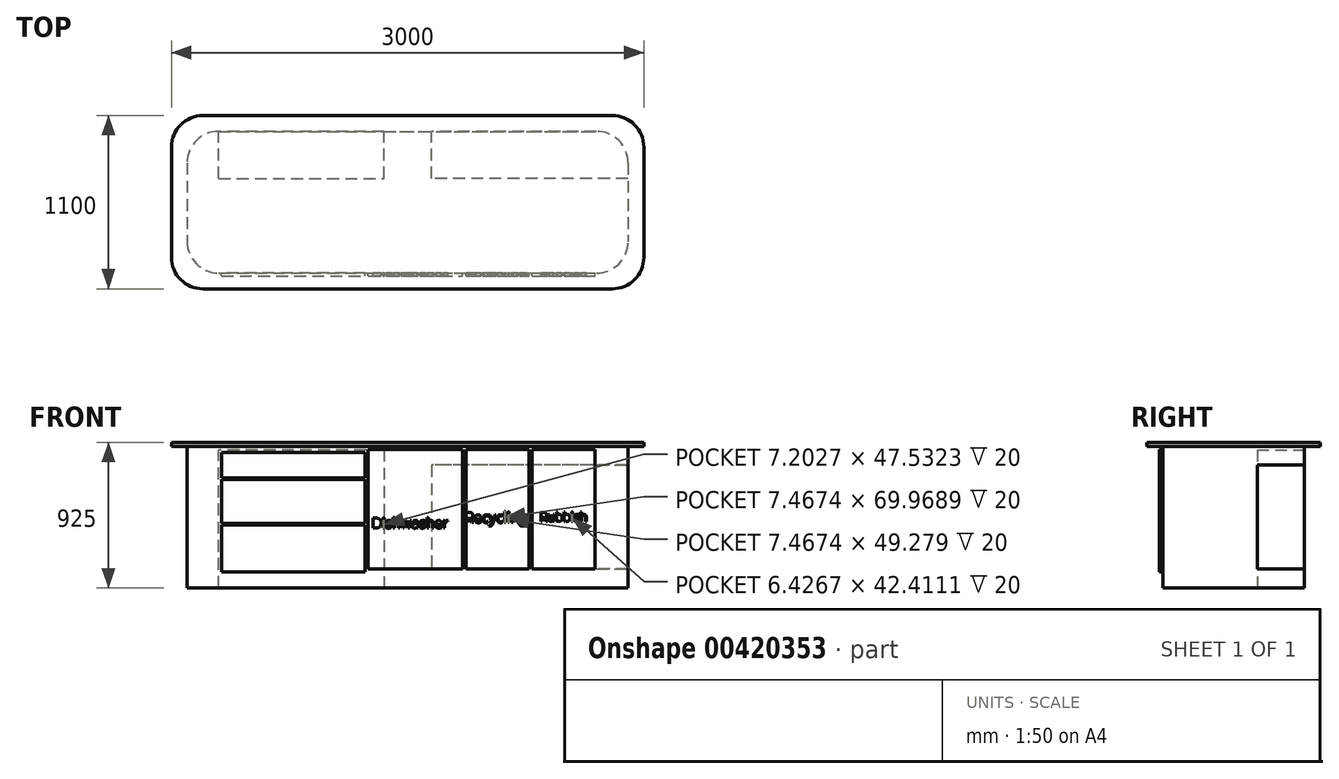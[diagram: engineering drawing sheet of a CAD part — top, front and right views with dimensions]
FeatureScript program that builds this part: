
annotation { "Feature Type Name" : "Feature", "Feature Type Description" : "" }
export const myFeature = defineFeature(function(context is Context, id is Id, definition is map)
    precondition{}
    {
        {
            var Q0;
            Q0=qCreatedBy(makeId("Top.planeOp"),FACE);
            var sketch = newSketch(context, id + "F0", { "sketchPlane" : qUnion([Q0])});
            skLineSegment(sketch, "E0", {"start": v(-1500, 0) * mm, "end": v(1500, 0) * mm, "construction": true});
            skLineSegment(sketch, "E1", {"start": v(0, 550) * mm, "end": v(0, -550) * mm, "construction": true});
            skLineSegment(sketch, "E2.bottom", {"start": v(-1300, 550) * mm, "end": v(1300, 550) * mm});
            skLineSegment(sketch, "E2.top", {"start": v(-1300, -550) * mm, "end": v(1300, -550) * mm});
            skLineSegment(sketch, "E2.left", {"start": v(-1500, 350) * mm, "end": v(-1500, -350) * mm});
            skLineSegment(sketch, "E2.right", {"start": v(1500, 350) * mm, "end": v(1500, -350) * mm});
            skPoint(sketch, "E3.visualSharp", {"position": v(-1500, 550) * mm});
            skPoint(sketch, "E4.visualSharp", {"position": v(1500, 550) * mm});
            skPoint(sketch, "E5.visualSharp", {"position": v(1500, -550) * mm});
            skPoint(sketch, "E6.visualSharp", {"position": v(-1500, -550) * mm});
            skLineSegment(sketch, "E7.bottom", {"start": v(-1200, 450) * mm, "end": v(1200, 450) * mm});
            skLineSegment(sketch, "E7.top", {"start": v(-1200, -450) * mm, "end": v(1200, -450) * mm});
            skLineSegment(sketch, "E7.left", {"start": v(-1400, 250) * mm, "end": v(-1400, -250) * mm});
            skLineSegment(sketch, "E7.right", {"start": v(1400, 250) * mm, "end": v(1400, -250) * mm});
            skPoint(sketch, "E8.visualSharp", {"position": v(1400, -450) * mm});
            skArc(sketch, "E8.filletArc", {"start": v(1200, -450) * mm, "mid": v(1341.42, -391.42) * mm, "end": v(1400, -250) * mm});
            skPoint(sketch, "E9.visualSharp", {"position": v(-1400, -450) * mm});
            skArc(sketch, "E9.filletArc", {"start": v(-1400, -250) * mm, "mid": v(-1341.42, -391.42) * mm, "end": v(-1200, -450) * mm});
            skPoint(sketch, "E10.visualSharp", {"position": v(1400, 450) * mm});
            skArc(sketch, "E10.filletArc", {"start": v(1400, 250) * mm, "mid": v(1341.42, 391.42) * mm, "end": v(1200, 450) * mm});
            skPoint(sketch, "E11.visualSharp", {"position": v(-1400, 450) * mm});
            skArc(sketch, "E11.filletArc", {"start": v(-1200, 450) * mm, "mid": v(-1341.42, 391.42) * mm, "end": v(-1400, 250) * mm});
            skArc(sketch, "E12.filletArc", {"start": v(1500, 350) * mm, "mid": v(1441.42, 491.42) * mm, "end": v(1300, 550) * mm});
            skArc(sketch, "E13.filletArc", {"start": v(1300, -550) * mm, "mid": v(1441.42, -491.42) * mm, "end": v(1500, -350) * mm});
            skArc(sketch, "E14.filletArc", {"start": v(-1500, -350) * mm, "mid": v(-1441.42, -491.42) * mm, "end": v(-1300, -550) * mm});
            skArc(sketch, "E15.filletArc", {"start": v(-1300, 550) * mm, "mid": v(-1441.42, 491.42) * mm, "end": v(-1500, 350) * mm});
            skSolve(sketch);
        }
        {
            var Q0;
            Q0=makeQuery(id+"F0.imprint","IMPRINT",FACE,{"disambiguationData":[TD([[makeQuery(id+"F0.imprint","IMPRINT",EDGE,{"derivedFrom":sQuery(id+"F0.wireOp",EDGE,"E7.bottom")}),-1.0]])]});
            extrude(context, id + "F1", {"entities" : qUnion([Q0]), "oppositeDirection" : true, "depth" : 900 * mm});
        }
        {
            var Q0;
            Q0=makeQuery(id+"F0.imprint","IMPRINT",FACE,{"disambiguationData":[TD([[makeQuery(id+"F0.imprint","IMPRINT",EDGE,{"derivedFrom":sQuery(id+"F0.wireOp",EDGE,"E2.bottom")}),-1.0]])]});
            var Q1;
            Q1=makeQuery(id+"F0.imprint","IMPRINT",FACE,{"disambiguationData":[TD([[makeQuery(id+"F0.imprint","IMPRINT",EDGE,{"derivedFrom":sQuery(id+"F0.wireOp",EDGE,"E7.bottom")}),-1.0]])]});
            extrude(context, id + "F2", {"entities" : qUnion([Q0, Q1]), "operationType" : NewBodyOperationType.ADD, "depth" : 25 * mm});
        }
        {
            var Q0;
            Q0=makeQuery(id+"F1.opExtrude","SWEPT_FACE",FACE,{"disambiguationData":[OSD([sQuery(id+"F0.wireOp",EDGE,"E7.top")])]});
            var sketch = newSketch(context, id + "F3", { "sketchPlane" : qUnion([Q0])});
            skLineSegment(sketch, "E16.bottom", {"start": v(-250, -20) * mm, "end": v(350, -20) * mm});
            skLineSegment(sketch, "E16.top", {"start": v(-250, -780) * mm, "end": v(350, -780) * mm});
            skLineSegment(sketch, "E16.left", {"start": v(-250, -20) * mm, "end": v(-250, -780) * mm});
            skLineSegment(sketch, "E16.right", {"start": v(350, -20) * mm, "end": v(350, -780) * mm});
            skLineSegment(sketch, "E17.bottom", {"start": v(-1160, -60) * mm, "end": v(-290, -60) * mm});
            skLineSegment(sketch, "E17.top", {"start": v(-1160, -180) * mm, "end": v(-290, -180) * mm});
            skLineSegment(sketch, "E17.left", {"start": v(-1160, -60) * mm, "end": v(-1160, -180) * mm});
            skLineSegment(sketch, "E17.right", {"start": v(-290, -60) * mm, "end": v(-290, -180) * mm});
            skLineSegment(sketch, "E18.bottom", {"start": v(-1160, -230) * mm, "end": v(-290, -230) * mm});
            skLineSegment(sketch, "E18.top", {"start": v(-1160, -470) * mm, "end": v(-290, -470) * mm});
            skLineSegment(sketch, "E18.left", {"start": v(-1160, -230) * mm, "end": v(-1160, -470) * mm});
            skLineSegment(sketch, "E18.right", {"start": v(-290, -230) * mm, "end": v(-290, -470) * mm});
            skLineSegment(sketch, "E19.bottom", {"start": v(-1160, -520) * mm, "end": v(-290, -520) * mm});
            skLineSegment(sketch, "E19.top", {"start": v(-1160, -780) * mm, "end": v(-290, -780) * mm});
            skLineSegment(sketch, "E19.left", {"start": v(-1160, -520) * mm, "end": v(-1160, -780) * mm});
            skLineSegment(sketch, "E19.right", {"start": v(-290, -520) * mm, "end": v(-290, -780) * mm});
            skLineSegment(sketch, "E20.bottom", {"start": v(-1180, -210) * mm, "end": v(-270, -210) * mm});
            skLineSegment(sketch, "E20.top", {"start": v(-1180, -490) * mm, "end": v(-270, -490) * mm});
            skLineSegment(sketch, "E20.left", {"start": v(-1180, -210) * mm, "end": v(-1180, -490) * mm});
            skLineSegment(sketch, "E20.right", {"start": v(-270, -210) * mm, "end": v(-270, -490) * mm});
            skLineSegment(sketch, "E21.bottom", {"start": v(-1180, -500) * mm, "end": v(-270, -500) * mm});
            skLineSegment(sketch, "E21.top", {"start": v(-1180, -800) * mm, "end": v(-270, -800) * mm});
            skLineSegment(sketch, "E21.left", {"start": v(-1180, -500) * mm, "end": v(-1180, -800) * mm});
            skLineSegment(sketch, "E21.right", {"start": v(-270, -500) * mm, "end": v(-270, -800) * mm});
            skLineSegment(sketch, "E22.bottom", {"start": v(-270, -200) * mm, "end": v(-1180, -200) * mm});
            skLineSegment(sketch, "E22.top", {"start": v(-270, -40) * mm, "end": v(-1180, -40) * mm});
            skLineSegment(sketch, "E22.left", {"start": v(-270, -200) * mm, "end": v(-270, -40) * mm});
            skLineSegment(sketch, "E22.right", {"start": v(-1180, -200) * mm, "end": v(-1180, -40) * mm});
            skLineSegment(sketch, "E23.bottom", {"start": v(-1200, -900) * mm, "end": v(-1200, -900) * mm});
            skLineSegment(sketch, "E23.top", {"start": v(-1200, -900) * mm, "end": v(-1200, -900) * mm});
            skLineSegment(sketch, "E23.left", {"start": v(-1200, -900) * mm, "end": v(-1200, -900) * mm});
            skLineSegment(sketch, "E23.right", {"start": v(-1200, -900) * mm, "end": v(-1200, -900) * mm});
            skLineSegment(sketch, "E24.top", {"start": v(-1200, -800) * mm, "end": v(-1200, -800) * mm});
            skLineSegment(sketch, "E24.left", {"start": v(-1200, -900) * mm, "end": v(-1200, -800) * mm});
            skLineSegment(sketch, "E24.right", {"start": v(-1200, -900) * mm, "end": v(-1200, -800) * mm});
            skText(sketch, "E25", { "text": "Dishwasher", "fontName": "OpenSans-Regular.ttf"});
            skLineSegment(sketch, "E26.bottom", {"start": v(370, -20) * mm, "end": v(770, -20) * mm});
            skLineSegment(sketch, "E26.top", {"start": v(370, -780) * mm, "end": v(770, -780) * mm});
            skLineSegment(sketch, "E26.left", {"start": v(370, -20) * mm, "end": v(370, -780) * mm});
            skLineSegment(sketch, "E26.right", {"start": v(770, -20) * mm, "end": v(770, -780) * mm});
            skLineSegment(sketch, "E27.bottom", {"start": v(790, -20) * mm, "end": v(1190, -20) * mm});
            skLineSegment(sketch, "E27.top", {"start": v(790, -780) * mm, "end": v(1190, -780) * mm});
            skLineSegment(sketch, "E27.left", {"start": v(790, -20) * mm, "end": v(790, -780) * mm});
            skLineSegment(sketch, "E27.right", {"start": v(1190, -20) * mm, "end": v(1190, -780) * mm});
            skText(sketch, "E28", { "text": "Recycling", "fontName": "OpenSans-Regular.ttf"});
            skText(sketch, "E29", { "text": "Rubbish", "fontName": "OpenSans-Regular.ttf"});
            const initialGuessF3  = {"E25": [-0.22795, -0.52, 1, 0, 0.06395], "E28": [0.36361, -0.48553, 1, 0, 0.0663], "E29": [0.84, -0.47629, 1, 0, 0.05706]};
            skSetInitialGuess(sketch, initialGuessF3);
            skSolve(sketch);
        }
        {
            var Q0;
            Q0=makeQuery(id+"F3.imprint","IMPRINT",FACE,{"disambiguationData":[TD([[makeQuery(id+"F3.imprint","IMPRINT",EDGE,{"derivedFrom":sQuery(id+"F3.wireOp",EDGE,"E16.bottom")}),-1.0]])]});
            var Q1;
            Q1=makeQuery(id+"F3.imprint","IMPRINT",FACE,{"disambiguationData":[TD([[makeQuery(id+"F3.imprint","IMPRINT",EDGE,{"derivedFrom":sQuery(id+"F3.wireOp",EDGE,"E26.bottom")}),-1.0]])]});
            var Q2;
            Q2=makeQuery(id+"F3.imprint","IMPRINT",FACE,{"disambiguationData":[TD([[makeQuery(id+"F3.imprint","IMPRINT",EDGE,{"derivedFrom":sQuery(id+"F3.wireOp",EDGE,"E27.bottom")}),-1.0]])]});
            var Q3;
            Q3=makeQuery(id+"F3.imprint","IMPRINT",FACE,{"disambiguationData":[TD([[makeQuery(id+"F3.imprint","IMPRINT",EDGE,{"derivedFrom":sQuery(id+"F3.wireOp",EDGE,"E18.bottom")}),-1.0]])]});
            var Q4;
            Q4=makeQuery(id+"F3.imprint","IMPRINT",FACE,{"disambiguationData":[TD([[makeQuery(id+"F3.imprint","IMPRINT",EDGE,{"derivedFrom":sQuery(id+"F3.wireOp",EDGE,"E17.bottom")}),-1.0]])]});
            var Q5;
            Q5=makeQuery(id+"F3.imprint","IMPRINT",FACE,{"disambiguationData":[TD([[makeQuery(id+"F3.imprint","IMPRINT",EDGE,{"derivedFrom":sQuery(id+"F3.wireOp",EDGE,"E19.bottom")}),-1.0]])]});
            var Q6;
            Q6=makeQuery(id+"F3.imprint","IMPRINT",FACE,{"disambiguationData":[TD([[makeQuery(id+"F3.imprint","IMPRINT",EDGE,{"derivedFrom":sQuery(id+"F3.wireOp",EDGE,"E19.bottom")}),1.0]])]});
            var Q7;
            Q7=makeQuery(id+"F3.imprint","IMPRINT",FACE,{"disambiguationData":[TD([[makeQuery(id+"F3.imprint","IMPRINT",EDGE,{"derivedFrom":sQuery(id+"F3.wireOp",EDGE,"E18.bottom")}),1.0]])]});
            var Q8;
            Q8=makeQuery(id+"F3.imprint","IMPRINT",FACE,{"disambiguationData":[TD([[makeQuery(id+"F3.imprint","IMPRINT",EDGE,{"derivedFrom":sQuery(id+"F3.wireOp",EDGE,"E17.bottom")}),1.0]])]});
            extrude(context, id + "F4", {"entities" : qUnion([Q0, Q1, Q2, Q3, Q4, Q5, Q6, Q7, Q8]), "operationType" : NewBodyOperationType.ADD, "depth" : 20 * mm});
        }
        {
            var Q0;
            Q0=makeQuery(id+"F1.opExtrude","SWEPT_FACE",FACE,{"disambiguationData":[OSD([sQuery(id+"F0.wireOp",EDGE,"E7.bottom")])]});
            var sketch = newSketch(context, id + "F5", { "sketchPlane" : qUnion([Q0])});
            skLineSegment(sketch, "E30.bottom", {"start": v(-1597.22, -120) * mm, "end": v(-151.4, -120) * mm});
            skLineSegment(sketch, "E30.top", {"start": v(-1597.22, -780) * mm, "end": v(-151.4, -780) * mm});
            skLineSegment(sketch, "E30.left", {"start": v(-1597.22, -120) * mm, "end": v(-1597.22, -780) * mm});
            skLineSegment(sketch, "E30.right", {"start": v(-151.4, -120) * mm, "end": v(-151.4, -780) * mm});
            skLineSegment(sketch, "E31.bottom", {"start": v(148.6, -22.24) * mm, "end": v(1200, -22.24) * mm});
            skLineSegment(sketch, "E31.top", {"start": v(148.6, -900) * mm, "end": v(1200, -900) * mm});
            skLineSegment(sketch, "E31.left", {"start": v(148.6, -22.24) * mm, "end": v(148.6, -900) * mm});
            skLineSegment(sketch, "E31.right", {"start": v(1200, -22.24) * mm, "end": v(1200, -900) * mm});
            skSolve(sketch);
        }
        {
            var Q0;
            Q0=makeQuery(id+"F5.imprint","IMPRINT",FACE,{"disambiguationData":[TD([[makeQuery(id+"F5.imprint","IMPRINT",EDGE,{"derivedFrom":sQuery(id+"F5.wireOp",EDGE,"E30.bottom")}),-1.0]])]});
            var Q1;
            Q1=makeQuery(id+"F5.imprint","IMPRINT",FACE,{"disambiguationData":[TD([[makeQuery(id+"F5.imprint","IMPRINT",EDGE,{"derivedFrom":sQuery(id+"F5.wireOp",EDGE,"E31.bottom")}),-1.0]])]});
            extrude(context, id + "F6", {"entities" : qUnion([Q0, Q1]), "operationType" : NewBodyOperationType.REMOVE, "oppositeDirection" : true, "depth" : 300 * mm});
        }
    });
